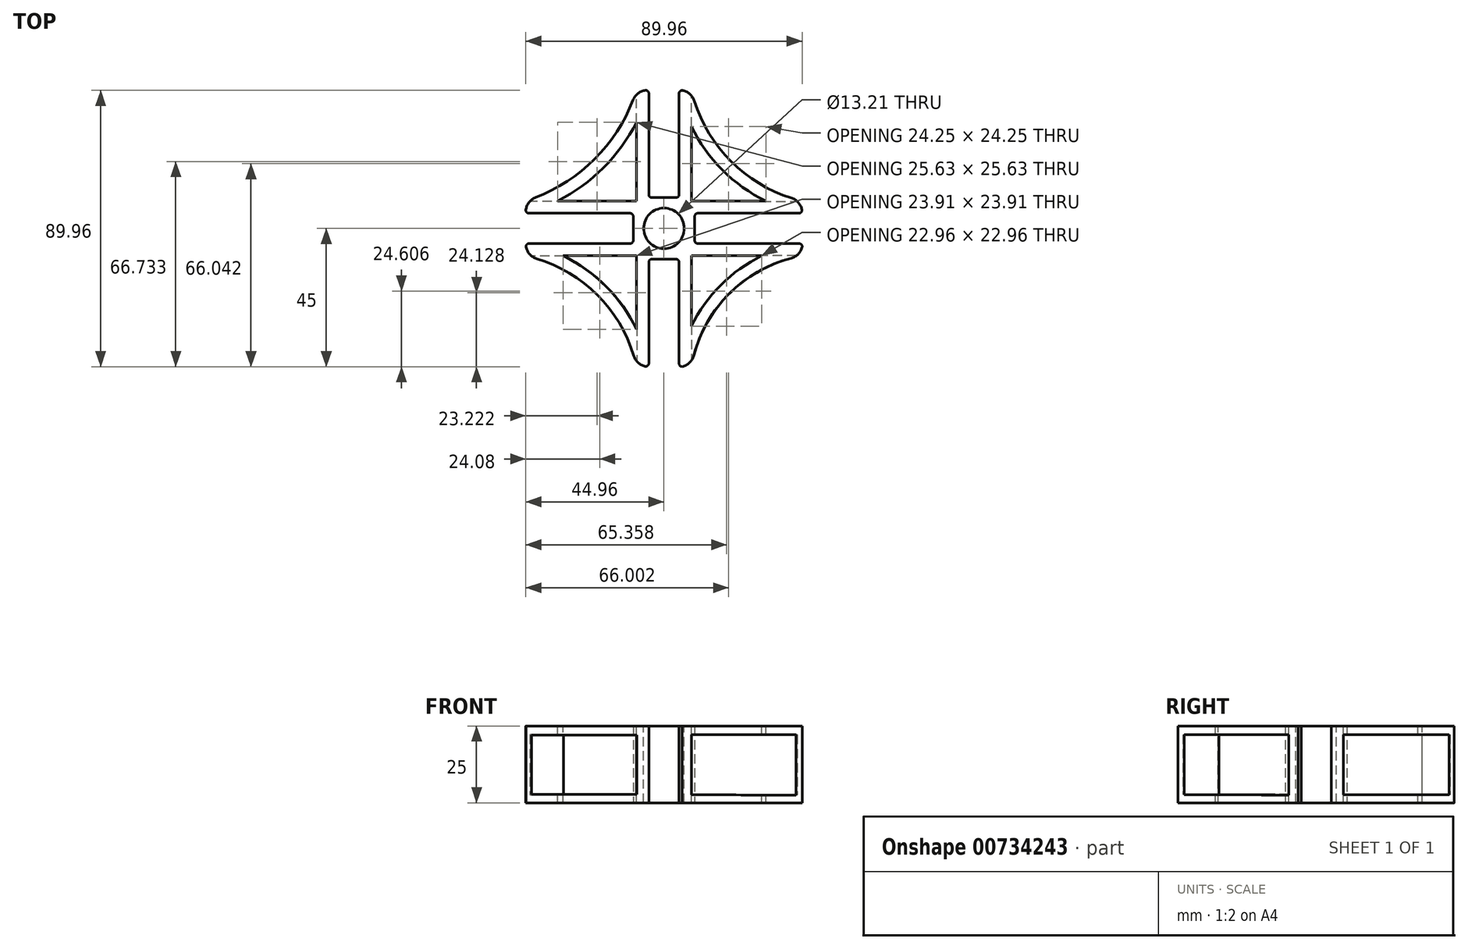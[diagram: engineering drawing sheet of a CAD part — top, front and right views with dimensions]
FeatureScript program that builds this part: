
annotation { "Feature Type Name" : "Feature", "Feature Type Description" : "" }
export const myFeature = defineFeature(function(context is Context, id is Id, definition is map)
    precondition{}
    {
        {
            var Q0;
            Q0=qCreatedBy(makeId("Top.planeOp"),FACE);
            var sketch = newSketch(context, id + "F0", { "sketchPlane" : qUnion([Q0])});
            skLineSegment(sketch, "E0.bottom", {"start": v(45, 45) * mm, "end": v(-45, 45) * mm, "construction": true});
            skLineSegment(sketch, "E0.top", {"start": v(45, -45) * mm, "end": v(-45, -45) * mm, "construction": true});
            skLineSegment(sketch, "E0.left", {"start": v(45, 45) * mm, "end": v(45, -45) * mm, "construction": true});
            skLineSegment(sketch, "E0.right", {"start": v(-45, 45) * mm, "end": v(-45, -45) * mm, "construction": true});
            skLineSegment(sketch, "E1", {"start": v(0, 45) * mm, "end": v(0, -45) * mm, "construction": true});
            skLineSegment(sketch, "E2", {"start": v(-45, 0) * mm, "end": v(45, 0) * mm, "construction": true});
            skLineSegment(sketch, "E3", {"start": v(-4.92, 45) * mm, "end": v(-4.92, -45) * mm, "construction": true});
            skLineSegment(sketch, "E4", {"start": v(4.92, 45) * mm, "end": v(4.92, -45) * mm, "construction": true});
            skLineSegment(sketch, "E5", {"start": v(-45, 4.92) * mm, "end": v(45, 4.92) * mm, "construction": true});
            skLineSegment(sketch, "E6", {"start": v(-45, -4.92) * mm, "end": v(45, -4.92) * mm, "construction": true});
            skLineSegment(sketch, "E7", {"start": v(-45, 4.92) * mm, "end": v(-45, 5.38) * mm});
            skLineSegment(sketch, "E8", {"start": v(-4.92, 45) * mm, "end": v(-5.38, 45) * mm});
            skLineSegment(sketch, "E9", {"start": v(4.92, 45) * mm, "end": v(5.12, 45) * mm});
            skLineSegment(sketch, "E10", {"start": v(45, 4.92) * mm, "end": v(45, 5.12) * mm});
            skLineSegment(sketch, "E11", {"start": v(45, -4.92) * mm, "end": v(45, -8.92) * mm});
            skLineSegment(sketch, "E12", {"start": v(-45, -4.92) * mm, "end": v(-45, -5.06) * mm});
            skLineSegment(sketch, "E13", {"start": v(-4.92, 45) * mm, "end": v(-4.92, 10) * mm});
            skLineSegment(sketch, "E14", {"start": v(-4.92, 10) * mm, "end": v(4.92, 10) * mm});
            skLineSegment(sketch, "E15", {"start": v(4.92, 10) * mm, "end": v(4.92, 45) * mm});
            skLineSegment(sketch, "E16", {"start": v(-4.92, -45) * mm, "end": v(-4.92, -10) * mm});
            skLineSegment(sketch, "E17", {"start": v(-4.92, -10) * mm, "end": v(4.92, -10) * mm});
            skLineSegment(sketch, "E18", {"start": v(4.92, -10) * mm, "end": v(4.92, -45) * mm});
            skLineSegment(sketch, "E19", {"start": v(45, -4.92) * mm, "end": v(10, -4.92) * mm});
            skLineSegment(sketch, "E20", {"start": v(10, -4.92) * mm, "end": v(10, 4.92) * mm});
            skLineSegment(sketch, "E21", {"start": v(10, 4.92) * mm, "end": v(45, 4.92) * mm});
            skLineSegment(sketch, "E22", {"start": v(-45, 4.92) * mm, "end": v(-10, 4.92) * mm});
            skLineSegment(sketch, "E23", {"start": v(-10, 4.92) * mm, "end": v(-10, -4.92) * mm});
            skLineSegment(sketch, "E24", {"start": v(-10, -4.92) * mm, "end": v(-45, -4.92) * mm});
            skLineSegment(sketch, "E25", {"start": v(-4.92, -45) * mm, "end": v(-5.06, -45) * mm});
            skLineSegment(sketch, "E26", {"start": v(4.92, -45) * mm, "end": v(8.92, -45) * mm});
            skArc(sketch, "E27", {"start": v(-41.8, 10.04) * mm, "mid": v(-22.56, 22.56) * mm, "end": v(-10.05, 41.8) * mm});
            skArc(sketch, "E28", {"start": v(9.88, 41.5) * mm, "mid": v(21.84, 21.84) * mm, "end": v(41.5, 9.88) * mm});
            skArc(sketch, "E29", {"start": v(45, -8.92) * mm, "mid": v(21.24, -21.24) * mm, "end": v(8.92, -45) * mm});
            skArc(sketch, "E30", {"start": v(-9.85, -41.44) * mm, "mid": v(-21.68, -21.68) * mm, "end": v(-41.45, -9.84) * mm});
            skPoint(sketch, "E31.visualSharp", {"position": v(-45, -8.92) * mm});
            skArc(sketch, "E31.filletArc", {"start": v(-45, -5.06) * mm, "mid": v(-44.01, -8.04) * mm, "end": v(-41.45, -9.84) * mm});
            skPoint(sketch, "E32.visualSharp", {"position": v(-8.92, -45) * mm});
            skArc(sketch, "E32.filletArc", {"start": v(-9.85, -41.44) * mm, "mid": v(-8.04, -44.01) * mm, "end": v(-5.06, -45) * mm});
            skPoint(sketch, "E33.visualSharp", {"position": v(45, 8.92) * mm});
            skArc(sketch, "E33.filletArc", {"start": v(45, 5.12) * mm, "mid": v(44.03, 8.07) * mm, "end": v(41.5, 9.88) * mm});
            skPoint(sketch, "E34.visualSharp", {"position": v(-45, 8.92) * mm});
            skArc(sketch, "E34.filletArc", {"start": v(-41.8, 10.04) * mm, "mid": v(-44.12, 8.2) * mm, "end": v(-45, 5.38) * mm});
            skPoint(sketch, "E35.visualSharp", {"position": v(-8.92, 45) * mm});
            skArc(sketch, "E35.filletArc", {"start": v(-5.38, 45) * mm, "mid": v(-8.21, 44.12) * mm, "end": v(-10.05, 41.8) * mm});
            skPoint(sketch, "E36.visualSharp", {"position": v(8.92, 45) * mm});
            skArc(sketch, "E36.filletArc", {"start": v(9.88, 41.5) * mm, "mid": v(8.07, 44.03) * mm, "end": v(5.12, 45) * mm});
            skSolve(sketch);
        }
        {
            var Q0;
            Q0 = qSketchRegion(id + "F0", true);
            extrude(context, id + "F1", {"entities" : qUnion([Q0]), "depth" : 25 * mm, "offsetDistance" : 25 * mm});
        }
        {
            var Q0;
            Q0=makeQuery(id+"F1.opExtrude","CAP_FACE",FACE,{"disambiguationData":[OSD([sQuery(id+"F0.wireOp",EDGE,"E7"),sQuery(id+"F0.wireOp",EDGE,"E8"),sQuery(id+"F0.wireOp",EDGE,"E9"),sQuery(id+"F0.wireOp",EDGE,"E10"),sQuery(id+"F0.wireOp",EDGE,"E11"),sQuery(id+"F0.wireOp",EDGE,"mrf3EofF-n60g-gq5k-HxXF-4o4gbP8yl62G"),sQuery(id+"F0.wireOp",EDGE,"WPb36Jyi-Yplt-UmGR-S4ml-xzFoEZJ1AGUH"),sQuery(id+"F0.wireOp",EDGE,"E12"),sQuery(id+"F0.wireOp",EDGE,"E13"),sQuery(id+"F0.wireOp",EDGE,"E14"),sQuery(id+"F0.wireOp",EDGE,"E15"),sQuery(id+"F0.wireOp",EDGE,"E16"),sQuery(id+"F0.wireOp",EDGE,"E17"),sQuery(id+"F0.wireOp",EDGE,"E18"),sQuery(id+"F0.wireOp",EDGE,"E19"),sQuery(id+"F0.wireOp",EDGE,"E20"),sQuery(id+"F0.wireOp",EDGE,"E21"),sQuery(id+"F0.wireOp",EDGE,"E22"),sQuery(id+"F0.wireOp",EDGE,"E23"),sQuery(id+"F0.wireOp",EDGE,"E24"),sQuery(id+"F0.wireOp",EDGE,"DmUrVjNc-OQAd-uyXZ-7e11-rqemhPKJUnGq"),sQuery(id+"F0.wireOp",EDGE,"iIeTaJyG-ahve-KeDB-Y1qS-69z2PehtN9Fa"),sQuery(id+"F0.wireOp",EDGE,"LsPioXYS-5SSy-yGGH-OOVc-X0c8Uvyni22l"),sQuery(id+"F0.wireOp",EDGE,"EEkTGBZt-yhL1-Odp7-P4UR-MFu5ju7VAFF7")])],"isStart":false});
            var sketch = newSketch(context, id + "F2", { "sketchPlane" : qUnion([Q0])});
            skCircle(sketch, "E37", {"center": v(0, 0) * mm, "radius": 6.6 * mm});
            skSolve(sketch);
        }
        {
            var Q0;
            Q0 = qSketchRegion(id + "F2", true);
            extrude(context, id + "F3", {"entities" : qUnion([Q0]), "operationType" : NewBodyOperationType.REMOVE, "oppositeDirection" : true, "depth" : 25 * mm, "offsetDistance" : 25 * mm});
        }
        {
            var Q0;
            Q0=makeQuery(id+"F1.opExtrude","SWEPT_FACE",FACE,{"disambiguationData":[OSD([sQuery(id+"F0.wireOp",EDGE,"E9")])]});
            var sketch = newSketch(context, id + "F4", { "sketchPlane" : qUnion([Q0])});
            skLineSegment(sketch, "E38.right", {"start": v(-52.2, 22.11) * mm, "end": v(-52.2, 2.6) * mm});
            skLineSegment(sketch, "E39.bottom", {"start": v(8.96, 22.11) * mm, "end": v(47.16, 22.11) * mm});
            skLineSegment(sketch, "E39.top", {"start": v(8.96, 2.6) * mm, "end": v(47.16, 2.6) * mm});
            skLineSegment(sketch, "E39.left", {"start": v(8.96, 22.11) * mm, "end": v(8.96, 2.6) * mm});
            skLineSegment(sketch, "E39.right", {"start": v(47.16, 22.11) * mm, "end": v(47.16, 2.6) * mm});
            skLineSegment(sketch, "E40", {"start": v(-52.2, 22.11) * mm, "end": v(-8.92, 22.11) * mm});
            skLineSegment(sketch, "E41", {"start": v(-8.92, 22.11) * mm, "end": v(-8.92, 2.6) * mm});
            skLineSegment(sketch, "E42", {"start": v(-8.92, 2.6) * mm, "end": v(-52.2, 2.6) * mm});
            skSolve(sketch);
        }
        {
            var Q0;
            Q0 = qSketchRegion(id + "F4", true);
            extrude(context, id + "F5", {"entities" : qUnion([Q0]), "operationType" : NewBodyOperationType.REMOVE, "oppositeDirection" : true, "depth" : 36.2 * mm, "offsetDistance" : 25 * mm});
        }
        {
            var Q0;
            Q0=makeQuery(id+"F1.opExtrude","SWEPT_EDGE",EDGE,{"disambiguationData":[OSD([sQuery(id+"F0.wireOp",EDGE,"E12"),sQuery(id+"F0.wireOp",EDGE,"E24")])]});
            var Q1;
            Q1=makeQuery(id+"F1.opExtrude","SWEPT_EDGE",EDGE,{"disambiguationData":[OSD([sQuery(id+"F0.wireOp",EDGE,"E7"),sQuery(id+"F0.wireOp",EDGE,"E22")])]});
            var Q2;
            Q2=makeQuery(id+"F1.opExtrude","SWEPT_EDGE",EDGE,{"disambiguationData":[OSD([sQuery(id+"F0.wireOp",EDGE,"WPb36Jyi-Yplt-UmGR-S4ml-xzFoEZJ1AGUH"),sQuery(id+"F0.wireOp",EDGE,"E16")])]});
            var Q3;
            Q3=makeQuery(id+"F1.opExtrude","SWEPT_EDGE",EDGE,{"disambiguationData":[OSD([sQuery(id+"F0.wireOp",EDGE,"mrf3EofF-n60g-gq5k-HxXF-4o4gbP8yl62G"),sQuery(id+"F0.wireOp",EDGE,"E18")])]});
            var Q4;
            Q4=makeQuery(id+"F1.opExtrude","SWEPT_EDGE",EDGE,{"disambiguationData":[OSD([sQuery(id+"F0.wireOp",EDGE,"E11"),sQuery(id+"F0.wireOp",EDGE,"E19")])]});
            var Q5;
            Q5=makeQuery(id+"F1.opExtrude","SWEPT_EDGE",EDGE,{"disambiguationData":[OSD([sQuery(id+"F0.wireOp",EDGE,"E10"),sQuery(id+"F0.wireOp",EDGE,"E21")])]});
            var Q6;
            Q6=makeQuery(id+"F1.opExtrude","SWEPT_EDGE",EDGE,{"disambiguationData":[OSD([sQuery(id+"F0.wireOp",EDGE,"E9"),sQuery(id+"F0.wireOp",EDGE,"E15")])]});
            var Q7;
            Q7=makeQuery(id+"F1.opExtrude","SWEPT_EDGE",EDGE,{"disambiguationData":[OSD([sQuery(id+"F0.wireOp",EDGE,"E8"),sQuery(id+"F0.wireOp",EDGE,"E13")])]});
            var Q8;
            Q8=makeQuery(id+"F1.opExtrude","SWEPT_EDGE",EDGE,{"disambiguationData":[OSD([sQuery(id+"F0.wireOp",EDGE,"E19"),sQuery(id+"F0.wireOp",EDGE,"E20")])]});
            var Q9;
            Q9=makeQuery(id+"F1.opExtrude","SWEPT_EDGE",EDGE,{"disambiguationData":[OSD([sQuery(id+"F0.wireOp",EDGE,"E20"),sQuery(id+"F0.wireOp",EDGE,"E21")])]});
            var Q10;
            Q10=makeQuery(id+"F1.opExtrude","SWEPT_EDGE",EDGE,{"disambiguationData":[OSD([sQuery(id+"F0.wireOp",EDGE,"E23"),sQuery(id+"F0.wireOp",EDGE,"E24")])]});
            var Q11;
            Q11=makeQuery(id+"F1.opExtrude","SWEPT_EDGE",EDGE,{"disambiguationData":[OSD([sQuery(id+"F0.wireOp",EDGE,"E22"),sQuery(id+"F0.wireOp",EDGE,"E23")])]});
            var Q12;
            Q12=makeQuery(id+"F1.opExtrude","SWEPT_EDGE",EDGE,{"disambiguationData":[OSD([sQuery(id+"F0.wireOp",EDGE,"E14"),sQuery(id+"F0.wireOp",EDGE,"E15")])]});
            var Q13;
            Q13=makeQuery(id+"F1.opExtrude","SWEPT_EDGE",EDGE,{"disambiguationData":[OSD([sQuery(id+"F0.wireOp",EDGE,"E13"),sQuery(id+"F0.wireOp",EDGE,"E14")])]});
            fillet(context, id + "F6", {"entities" : qUnion([Q0, Q1, Q2, Q3, Q4, Q5, Q6, Q7, Q8, Q9, Q10, Q11, Q12, Q13]), "radius" : 1 * mm, "tangentPropagation" : true, "allowEdgeOverflow" : false});
        }
        {
            var Q0;
            Q0=makeQuery(id+"F1.opExtrude","CAP_FACE",FACE,{"disambiguationData":[OSD([sQuery(id+"F0.wireOp",EDGE,"E7"),sQuery(id+"F0.wireOp",EDGE,"E8"),sQuery(id+"F0.wireOp",EDGE,"E9"),sQuery(id+"F0.wireOp",EDGE,"E10"),sQuery(id+"F0.wireOp",EDGE,"E11"),sQuery(id+"F0.wireOp",EDGE,"E12"),sQuery(id+"F0.wireOp",EDGE,"E13"),sQuery(id+"F0.wireOp",EDGE,"E14"),sQuery(id+"F0.wireOp",EDGE,"E15"),sQuery(id+"F0.wireOp",EDGE,"E16"),sQuery(id+"F0.wireOp",EDGE,"E17"),sQuery(id+"F0.wireOp",EDGE,"E18"),sQuery(id+"F0.wireOp",EDGE,"E19"),sQuery(id+"F0.wireOp",EDGE,"E20"),sQuery(id+"F0.wireOp",EDGE,"E21"),sQuery(id+"F0.wireOp",EDGE,"E22"),sQuery(id+"F0.wireOp",EDGE,"E23"),sQuery(id+"F0.wireOp",EDGE,"E24"),sQuery(id+"F0.wireOp",EDGE,"E25"),sQuery(id+"F0.wireOp",EDGE,"E26"),sQuery(id+"F0.wireOp",EDGE,"E27"),sQuery(id+"F0.wireOp",EDGE,"E28"),sQuery(id+"F0.wireOp",EDGE,"E29"),sQuery(id+"F0.wireOp",EDGE,"E30")])],"isStart":false});
            var sketch = newSketch(context, id + "F7", { "sketchPlane" : qUnion([Q0])});
            skLineSegment(sketch, "E43.5", {"start": v(-34.55, 8.92) * mm, "end": v(-8.92, 8.92) * mm});
            skLineSegment(sketch, "E43.6", {"start": v(8.92, 8.92) * mm, "end": v(33.17, 8.92) * mm});
            skArc(sketch, "E43.8", {"start": v(-8.92, 34.55) * mm, "mid": v(-19.74, 19.73) * mm, "end": v(-34.55, 8.92) * mm});
            skLineSegment(sketch, "E43.9", {"start": v(8.92, 33.17) * mm, "end": v(8.92, 8.92) * mm});
            skLineSegment(sketch, "E43.12", {"start": v(-8.92, 8.92) * mm, "end": v(-8.92, 34.55) * mm});
            skArc(sketch, "E43.13", {"start": v(33.17, 8.92) * mm, "mid": v(19, 19) * mm, "end": v(8.92, 33.17) * mm});
            skLineSegment(sketch, "E44", {"start": v(-8.92, -8.92) * mm, "end": v(-8.92, -32.83) * mm});
            skLineSegment(sketch, "E45", {"start": v(8.92, -8.92) * mm, "end": v(31.88, -8.92) * mm});
            skLineSegment(sketch, "E46", {"start": v(-8.92, -8.92) * mm, "end": v(-32.84, -8.92) * mm});
            skLineSegment(sketch, "E47", {"start": v(8.92, -8.92) * mm, "end": v(8.92, -31.87) * mm});
            skArc(sketch, "E48", {"start": v(-8.92, -32.83) * mm, "mid": v(-18.87, -18.86) * mm, "end": v(-32.84, -8.92) * mm});
            skArc(sketch, "E49", {"start": v(31.88, -8.92) * mm, "mid": v(18.47, -18.47) * mm, "end": v(8.92, -31.87) * mm});
            skSolve(sketch);
        }
        {
            var Q0;
            Q0=makeQuery(id+"F7.imprint","IMPRINT",FACE,{"disambiguationData":[TD([[makeQuery(id+"F7.imprint","IMPRINT",EDGE,{"derivedFrom":sQuery(id+"F7.wireOp",EDGE,"E43.6")}),1.0]])]});
            var Q1;
            Q1=makeQuery(id+"F7.imprint","IMPRINT",FACE,{"disambiguationData":[TD([[makeQuery(id+"F7.imprint","IMPRINT",EDGE,{"derivedFrom":sQuery(id+"F7.wireOp",EDGE,"E43.5")}),1.0]])]});
            var Q2;
            Q2=makeQuery(id+"F7.imprint","IMPRINT",FACE,{"disambiguationData":[TD([[makeQuery(id+"F7.imprint","IMPRINT",EDGE,{"derivedFrom":sQuery(id+"F7.wireOp",EDGE,"E43.7")}),1.0]])]});
            var Q3;
            Q3=makeQuery(id+"F7.imprint","IMPRINT",FACE,{"disambiguationData":[TD([[makeQuery(id+"F7.imprint","IMPRINT",EDGE,{"derivedFrom":sQuery(id+"F7.wireOp",EDGE,"E43.1")}),1.0]])]});
            extrude(context, id + "F8", {"entities" : qUnion([Q0, Q1, Q2, Q3]), "operationType" : NewBodyOperationType.REMOVE, "oppositeDirection" : true, "depth" : 25 * mm, "offsetDistance" : 25 * mm});
        }
        {
            var Q0;
            Q0=makeQuery(id+"F1.opExtrude","SWEPT_FACE",FACE,{"disambiguationData":[OSD([sQuery(id+"F0.wireOp",EDGE,"E26")])]});
            var sketch = newSketch(context, id + "F9", { "sketchPlane" : qUnion([Q0])});
            skLineSegment(sketch, "E50.bottom", {"start": v(-8.81, 22.1) * mm, "end": v(-46.99, 22.1) * mm});
            skLineSegment(sketch, "E50.top", {"start": v(-8.81, 2.7) * mm, "end": v(-46.99, 2.7) * mm});
            skLineSegment(sketch, "E50.left", {"start": v(-8.81, 22.1) * mm, "end": v(-8.81, 2.7) * mm});
            skLineSegment(sketch, "E50.right", {"start": v(-46.99, 22.1) * mm, "end": v(-46.99, 2.7) * mm});
            skLineSegment(sketch, "E51.right", {"start": v(55, 22.2) * mm, "end": v(55, 2.46) * mm});
            skLineSegment(sketch, "E52", {"start": v(55, 22.2) * mm, "end": v(9, 22.11) * mm});
            skLineSegment(sketch, "E53", {"start": v(9, 22.11) * mm, "end": v(9, 2.6) * mm});
            skLineSegment(sketch, "E54", {"start": v(9, 2.6) * mm, "end": v(55, 2.46) * mm});
            skSolve(sketch);
        }
        {
            var Q0;
            Q0=makeQuery(id+"F9.imprint","IMPRINT",FACE,{"disambiguationData":[TD([[makeQuery(id+"F9.imprint","IMPRINT",EDGE,{"derivedFrom":sQuery(id+"F9.wireOp",EDGE,"E50.bottom")}),1.0]])]});
            var Q1;
            Q1=makeQuery(id+"F9.imprint","IMPRINT",FACE,{"disambiguationData":[TD([[makeQuery(id+"F9.imprint","IMPRINT",EDGE,{"derivedFrom":sQuery(id+"F9.wireOp",EDGE,"E51.bottom")}),-1.0]])]});
            var Q2;
            {var subQ3=sQuery(id+"F9.wireOp",EDGE,"yZ7sxOcy-J3CI-yWzy-BjE7-O1ItGjDutbW9");Q2=makeQuery(id+"F9.imprint","IMPRINT",FACE,{"disambiguationData":[TD([[makeQuery(id+"F9.imprint","IMPRINT",EDGE,{"derivedFrom":subQ3}),-1.0]])]});}
            extrude(context, id + "F10", {"entities" : qUnion([Q0, Q1, Q2]), "operationType" : NewBodyOperationType.REMOVE, "oppositeDirection" : true, "depth" : 36 * mm, "offsetDistance" : 25 * mm});
        }
        {
            var Q0;
            Q0=makeQuery(id+"F7.imprint","IMPRINT",FACE,{"disambiguationData":[TD([[makeQuery(id+"F7.imprint","IMPRINT",EDGE,{"derivedFrom":sQuery(id+"F7.wireOp",EDGE,"E45")}),-1.0]])]});
            var Q1;
            Q1=makeQuery(id+"F7.imprint","IMPRINT",FACE,{"disambiguationData":[TD([[makeQuery(id+"F7.imprint","IMPRINT",EDGE,{"derivedFrom":sQuery(id+"F7.wireOp",EDGE,"E44")}),-1.0]])]});
            extrude(context, id + "F11", {"entities" : qUnion([Q0, Q1]), "operationType" : NewBodyOperationType.REMOVE, "oppositeDirection" : true, "depth" : 25 * mm, "offsetDistance" : 25 * mm});
        }
        {
            var Q0;
            Q0=makeQuery(id+"F1.opExtrude","SWEPT_EDGE",EDGE,{"disambiguationData":[OSD([sQuery(id+"F0.wireOp",EDGE,"E11"),sQuery(id+"F0.wireOp",EDGE,"E29")])]});
            fillet(context, id + "F12", {"entities" : qUnion([Q0]), "radius" : 5 * mm, "tangentPropagation" : true, "allowEdgeOverflow" : false});
        }
        {
            var Q0;
            Q0=makeQuery(id+"F9.imprint","IMPRINT",FACE,{"disambiguationData":[TD([[makeQuery(id+"F9.imprint","IMPRINT",EDGE,{"derivedFrom":sQuery(id+"F9.wireOp",EDGE,"E51.right")}),-1.0]])]});
            extrude(context, id + "F13", {"entities" : qUnion([Q0]), "operationType" : NewBodyOperationType.REMOVE, "oppositeDirection" : true, "depth" : 36.08 * mm, "offsetDistance" : 25 * mm});
        }
        {
            var Q0;
            Q0=makeQuery(id+"F9.imprint","IMPRINT",FACE,{"disambiguationData":[TD([[makeQuery(id+"F9.imprint","IMPRINT",EDGE,{"derivedFrom":sQuery(id+"F9.wireOp",EDGE,"E51.right")}),-1.0]])]});
            extrude(context, id + "F14", {"entities" : qUnion([Q0]), "operationType" : NewBodyOperationType.REMOVE, "oppositeDirection" : true, "depth" : 36.04 * mm, "offsetDistance" : 25 * mm});
        }
        {
            var Q0;
            Q0=makeQuery(id+"F1.opExtrude","SWEPT_EDGE",EDGE,{"disambiguationData":[OSD([sQuery(id+"F0.wireOp",EDGE,"E26"),sQuery(id+"F0.wireOp",EDGE,"E29")])]});
            fillet(context, id + "F15", {"entities" : qUnion([Q0]), "radius" : 5 * mm, "tangentPropagation" : true, "allowEdgeOverflow" : false});
        }
    });
